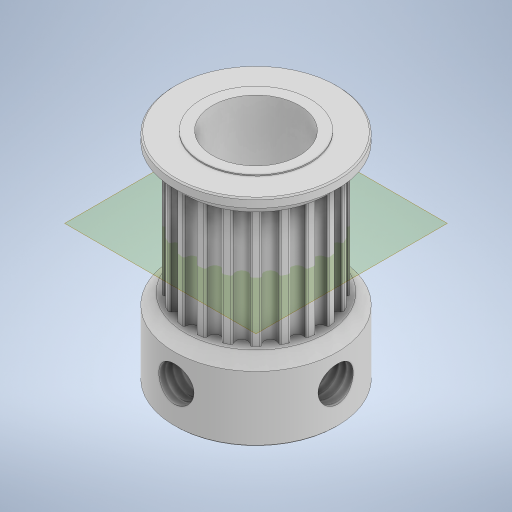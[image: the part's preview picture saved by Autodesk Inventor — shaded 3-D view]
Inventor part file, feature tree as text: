
AUTODESK INVENTOR PART (.ipt)
format: ipt  version: 2024 (Build 280153000, 153)  size: 451,584 bytes
history: native  units: mm
features: plane x4, extrude x2, mirror x2, chamfer x2, projected_geometry x2, revolve x1, hole x1, pattern_circular x1
ambient origin geometry x8: Origin, YZ Plane, XZ Plane, XY Plane, X Axis, Y Axis, Z Axis, Center Point
bodies: Solid1 (feature_tree)
feature tree (15):
  revolve  "Revolution1"  [1 undecoded]
  extrude  "Extrusion1"  Depth=4.0mm
  plane  "Work Plane1"
  mirror  "Mirror1"
  chamfer  "Chamfer2"  Distance=20.0mm
  chamfer  "Chamfer1"  Distance=11.0mm
  plane  "Work Plane2"
  hole  "Hole1"  [1 undecoded]
  plane  "Work Plane3"
  mirror  "Mirror2"
  extrude  "Extrusion2"  Depth=6.11mm
  pattern_circular  "Circular Pattern1"  Angle=90.0deg  [1 undecoded]
  plane  "Work Plane4"
  projected_geometry  "Projected Loop1"
  projected_geometry  "Project Cut Edges2"
note: 3 required parameter values undecoded (feature->parameter linkage not recoverable at this tier; creation-order binding heuristic only, values carry confidence <= 0.55)